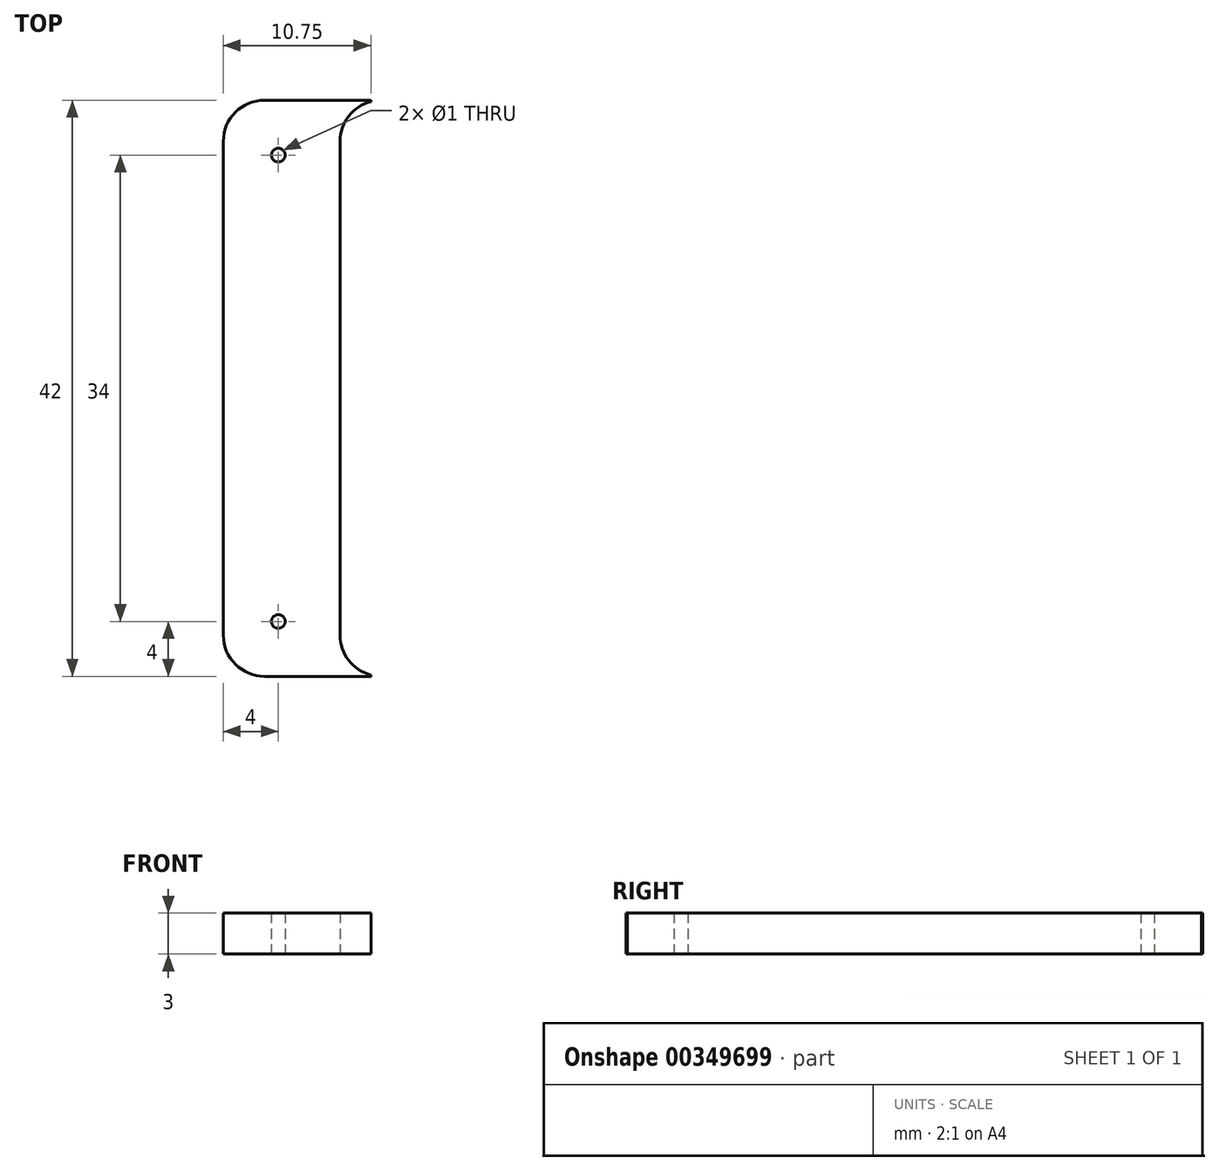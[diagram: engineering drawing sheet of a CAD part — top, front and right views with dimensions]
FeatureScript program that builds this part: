
annotation { "Feature Type Name" : "Feature", "Feature Type Description" : "" }
export const myFeature = defineFeature(function(context is Context, id is Id, definition is map)
    precondition{}
    {
        {
            var Q0;
            Q0=qCreatedBy(makeId("Top.planeOp"),FACE);
            var sketch = newSketch(context, id + "F0", { "sketchPlane" : qUnion([Q0])});
            skLineSegment(sketch, "E0.bottom", {"start": v(10, 0) * mm, "end": v(10.75, 0) * mm});
            skLineSegment(sketch, "E0.top", {"start": v(10, 42) * mm, "end": v(10.75, 42) * mm});
            skLineSegment(sketch, "E0.left", {"start": v(0, 3) * mm, "end": v(0, 39) * mm});
            skLineSegment(sketch, "E1", {"start": v(8.5, 39) * mm, "end": v(8.5, 3) * mm});
            skPoint(sketch, "E2.visualSharp", {"position": v(0, 42) * mm});
            skArc(sketch, "E2.filletArc", {"start": v(3, 42) * mm, "mid": v(0.88, 41.12) * mm, "end": v(0, 39) * mm});
            skPoint(sketch, "E3.visualSharp", {"position": v(0, 0) * mm});
            skArc(sketch, "E3.filletArc", {"start": v(0, 3) * mm, "mid": v(0.88, 0.88) * mm, "end": v(3, 0) * mm});
            skArc(sketch, "E4.filletArc", {"start": v(10.75, 41.9) * mm, "mid": v(9.13, 40.84) * mm, "end": v(8.5, 39) * mm});
            skArc(sketch, "E5.filletArc", {"start": v(8.5, 3) * mm, "mid": v(9.13, 1.16) * mm, "end": v(10.75, 0.1) * mm});
            skLineSegment(sketch, "E6", {"start": v(3, 42) * mm, "end": v(10.75, 42) * mm});
            skLineSegment(sketch, "E7", {"start": v(3, 0) * mm, "end": v(10.75, 0) * mm});
            skLineSegment(sketch, "E8", {"start": v(10.75, 42) * mm, "end": v(10.75, 41.9) * mm});
            skPoint(sketch, "E8.startSnap0", {"position": v(10.75, 42) * mm});
            skPoint(sketch, "E9.orphan", {"position": v(10.75, 50.78) * mm});
            skPoint(sketch, "E10.orphan", {"position": v(11.5, 42) * mm});
            skLineSegment(sketch, "E11.trimOffspring", {"start": v(10.75, 0.1) * mm, "end": v(10.75, 0) * mm});
            skSolve(sketch);
        }
        {
            var Q0;
            Q0=makeQuery(id+"F0.imprint","IMPRINT",FACE,{"disambiguationData":[TD([[makeQuery(id+"F0.imprint","IMPRINT",EDGE,{"derivedFrom":sQuery(id+"F0.wireOp",EDGE,"E0.left")}),-1.0]])]});
            extrude(context, id + "F1", {"entities" : qUnion([Q0]), "depth" : 3 * mm});
        }
        {
            var Q0;
            Q0=makeQuery(id+"F1.opExtrude","CAP_FACE",FACE,{"disambiguationData":[OSD([sQuery(id+"F0.wireOp",EDGE,"E0.left"),sQuery(id+"F0.wireOp",EDGE,"E1"),sQuery(id+"F0.wireOp",EDGE,"E2.filletArc"),sQuery(id+"F0.wireOp",EDGE,"E3.filletArc"),sQuery(id+"F0.wireOp",EDGE,"E4.filletArc"),sQuery(id+"F0.wireOp",EDGE,"E5.filletArc"),sQuery(id+"F0.wireOp",EDGE,"E6"),sQuery(id+"F0.wireOp",EDGE,"E7"),sQuery(id+"F0.wireOp",EDGE,"E8"),sQuery(id+"F0.wireOp",EDGE,"E11.trimOffspring")])],"isStart":false});
            var sketch = newSketch(context, id + "F2", { "sketchPlane" : qUnion([Q0])});
            skPoint(sketch, "E12", {"position": v(4, 4) * mm});
            skPoint(sketch, "E13", {"position": v(4, 38) * mm});
            skSolve(sketch);
        }
        {
            var Q0;
            Q0=sQuery(id+"F2.wireOp",VERTEX,"E13");
            var Q1;
            Q1=sQuery(id+"F2.wireOp",VERTEX,"E12");
            var Q2;
            Q2=makeQuery(id+"F1.opExtrude","SWEPT_BODY",BODY,{"disambiguationData":[OSD([sQuery(id+"F0.wireOp",EDGE,"E0.left"),sQuery(id+"F0.wireOp",EDGE,"E1"),sQuery(id+"F0.wireOp",EDGE,"E2.filletArc"),sQuery(id+"F0.wireOp",EDGE,"E3.filletArc"),sQuery(id+"F0.wireOp",EDGE,"E4.filletArc"),sQuery(id+"F0.wireOp",EDGE,"E5.filletArc"),sQuery(id+"F0.wireOp",EDGE,"E6"),sQuery(id+"F0.wireOp",EDGE,"E7"),sQuery(id+"F0.wireOp",EDGE,"E8"),sQuery(id+"F0.wireOp",EDGE,"E11.trimOffspring")])]});
            hole(context, id + "F3", {"style" : HoleStyle.SIMPLE, "endStyle" : HoleEndStyle.THROUGH, "holeDiameter" : 1 * mm, "isTappedThrough" : true, "tappedDepth" : 12 * mm, "tapClearance" : 3, "locations" : qUnion([Q0, Q1]), "scope" : qUnion([Q2])});
        }
    });
